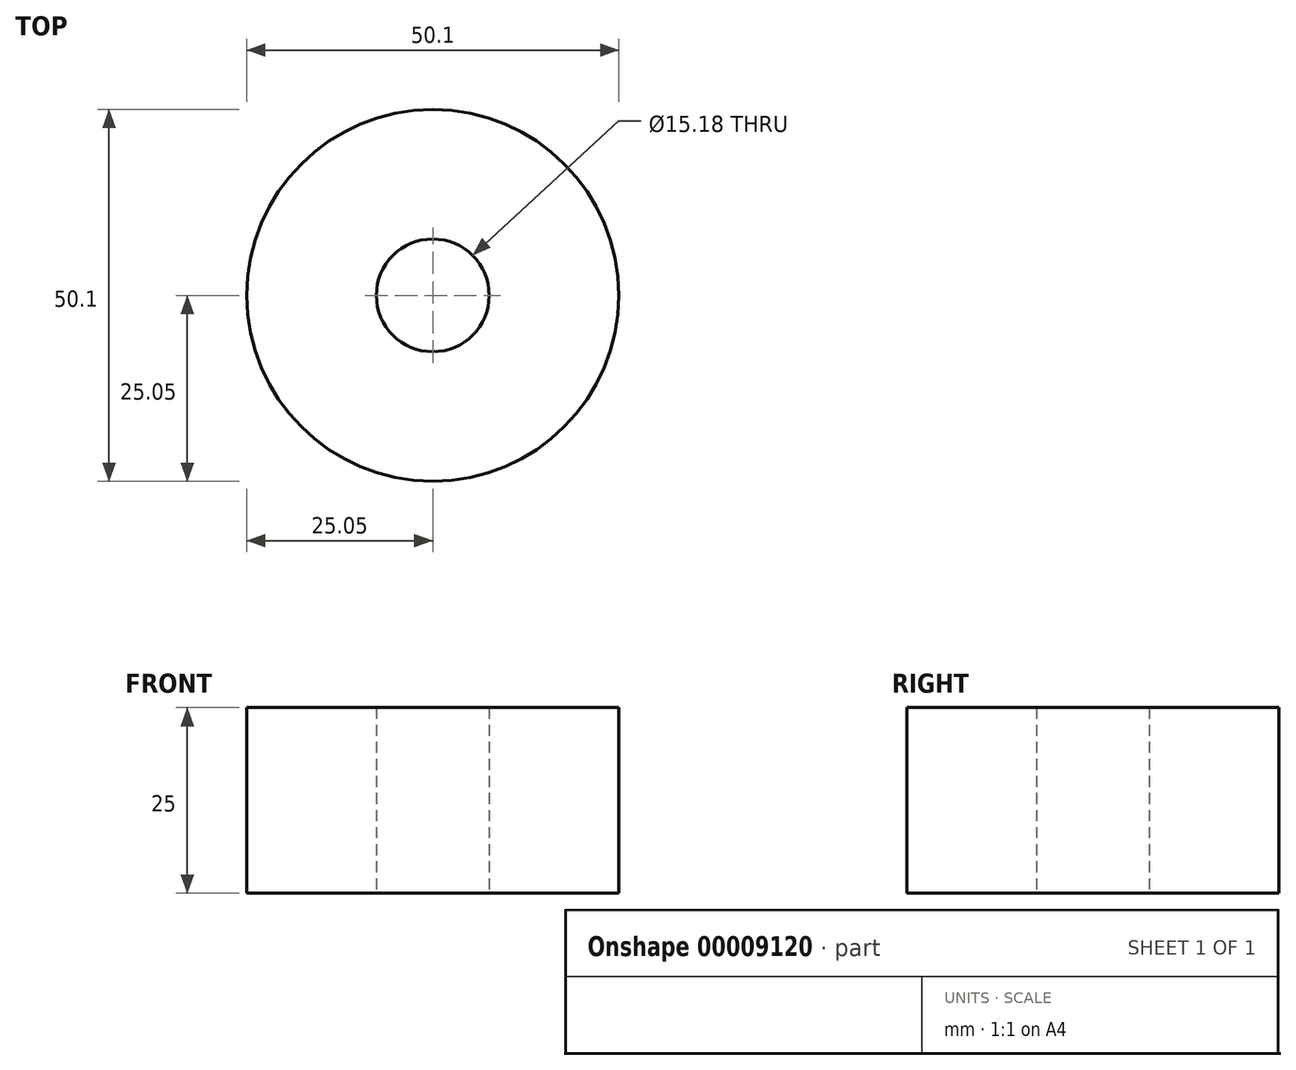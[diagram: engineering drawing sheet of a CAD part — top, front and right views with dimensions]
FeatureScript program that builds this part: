
annotation { "Feature Type Name" : "Feature", "Feature Type Description" : "" }
export const myFeature = defineFeature(function(context is Context, id is Id, definition is map)
    precondition{}
    {
        {
            var Q0;
            Q0=qCreatedBy(makeId("Top.planeOp"),FACE);
            var sketch = newSketch(context, id + "F0", { "sketchPlane" : qUnion([Q0])});
            skCircle(sketch, "E0", {"center": v(0, 0) * mm, "radius": 25.05 * mm});
            skSolve(sketch);
        }
        {
            var Q0;
            Q0 = qSketchRegion(id + "F0", true);
            extrude(context, id + "F1", {"entities" : qUnion([Q0]), "depth" : 25 * mm});
        }
        {
            var Q0;
            Q0=qCreatedBy(makeId("Top.planeOp"),FACE);
            var sketch = newSketch(context, id + "F2", { "sketchPlane" : qUnion([Q0])});
            skCircle(sketch, "E1", {"center": v(0, 0) * mm, "radius": 7.6 * mm});
            skSolve(sketch);
        }
        {
            var Q0;
            Q0 = qSketchRegion(id + "F2", true);
            extrude(context, id + "F3", {"entities" : qUnion([Q0]), "depth" : 50 * mm});
        }
        {
            var Q0;
            Q0=makeQuery(id+"F3.opExtrude","SWEPT_BODY",BODY,{"disambiguationData":[OSD([sQuery(id+"F2.wireOp",EDGE,"E1")])]});
            var Q1;
            Q1=makeQuery(id+"F1.opExtrude","SWEPT_BODY",BODY,{"disambiguationData":[OSD([sQuery(id+"F0.wireOp",EDGE,"E0")])]});
            booleanBodies(context, id + "F4", {"operationType" : BooleanOperationType.SUBTRACTION, "tools" : qUnion([Q0]), "targets" : qUnion([Q1])});
        }
    });
